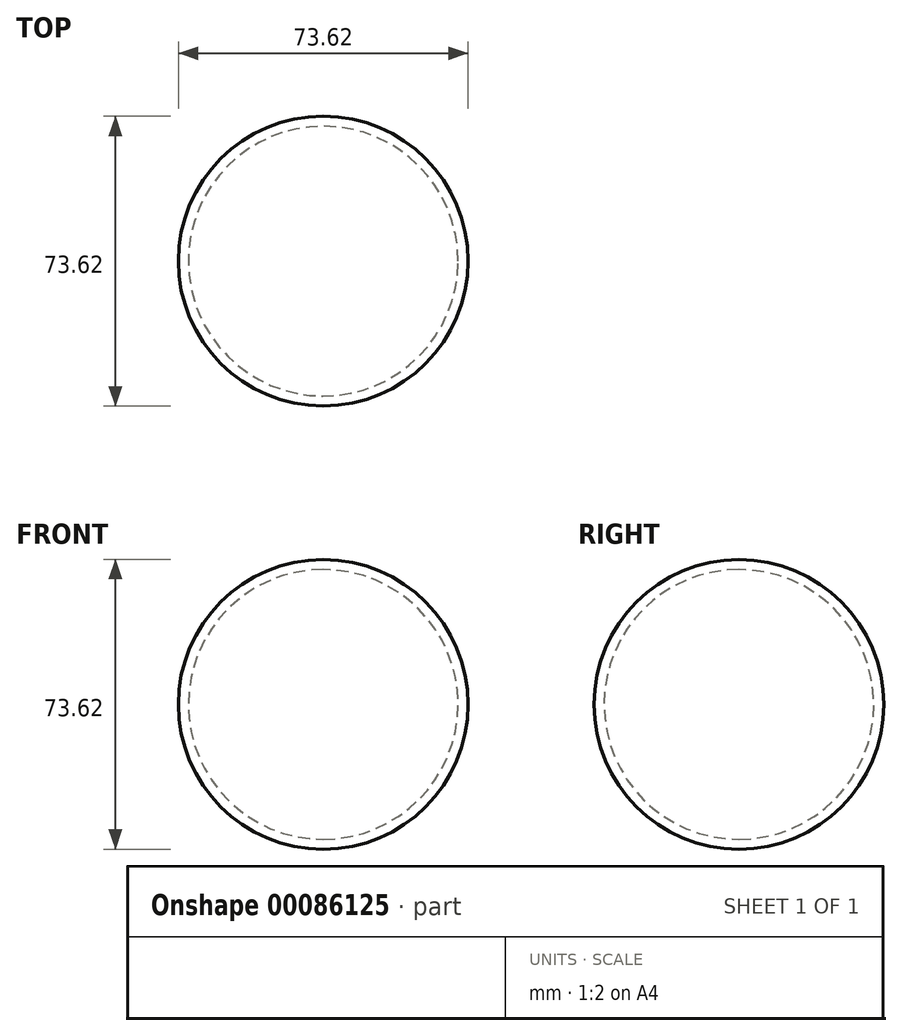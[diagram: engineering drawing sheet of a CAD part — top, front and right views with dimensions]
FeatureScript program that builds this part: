
annotation { "Feature Type Name" : "Feature", "Feature Type Description" : "" }
export const myFeature = defineFeature(function(context is Context, id is Id, definition is map)
    precondition{}
    {
        {
            var Q0;
            Q0=qCreatedBy(makeId("Right.planeOp"),FACE);
            var sketch = newSketch(context, id + "F0", { "sketchPlane" : qUnion([Q0])});
            skCircle(sketch, "E0", {"center": v(0, 0) * mm, "radius": 36.8 * mm});
            skLineSegment(sketch, "E1", {"start": v(0, 36.8) * mm, "end": v(0, -36.8) * mm});
            skSolve(sketch);
        }
        {
            var Q0;
            {var subQ0=sQuery(id+"F0.wireOp",EDGE,"E1");Q0=makeQuery(id+"F0.imprint","IMPRINT",FACE,{"disambiguationData":[TD([[makeQuery(id+"F0.imprint","IMPRINT",EDGE,{"derivedFrom":subQ0}),-1.0]])]});}
            var Q1;
            Q1=sQuery(id+"F0.wireOp",EDGE,"E1");
            revolve(context, id + "F1", {"entities" : qUnion([Q0]), "axis" : qUnion([Q1]), "revolveType" : RevolveType.FULL});
        }
        {
            var Q0;
            Q0=qCreatedBy(makeId("Front.planeOp"),FACE);
            var sketch = newSketch(context, id + "F2", { "sketchPlane" : qUnion([Q0])});
            skCircle(sketch, "E2", {"center": v(-11.25, 16.75) * mm, "radius": 7.86 * mm});
            skCircle(sketch, "E3", {"center": v(11.01, 16.75) * mm, "radius": 8.23 * mm});
            skSolve(sketch);
        }
        {
            var Q0;
            Q0=sQuery(id+"F2.wireOp",EDGE,"E2");
            var Q1;
            Q1=sQuery(id+"F2.wireOp",EDGE,"E3");
            extrude(context, id + "F3", {"bodyType" : ToolBodyType.SURFACE, "surfaceEntities" : qUnion([Q0, Q1]), "depth" : 40.82 * mm});
        }
        {
            var Q0;
            Q0=makeQuery(id+"F1.opRevolve","SWEPT_FACE",FACE,{"disambiguationData":[OSD([sQuery(id+"F0.wireOp",EDGE,"E0")])]});
            var Q1;
            Q1=makeQuery(id+"F1.opRevolve","SWEPT_BODY",BODY,{"disambiguationData":[OSD([sQuery(id+"F0.wireOp",EDGE,"E0"),sQuery(id+"F0.wireOp",EDGE,"E1")])]});
            shell(context, id + "F4", {"isHollow" : true, "entities" : qUnion([Q0]), "parts" : qUnion([Q1]), "thickness" : 2.54 * mm});
        }
    });
